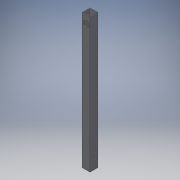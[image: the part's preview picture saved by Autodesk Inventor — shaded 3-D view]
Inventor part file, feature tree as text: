
AUTODESK INVENTOR PART (.ipt)
format: ipt  version: 2018 (Build 220112000, 112)  size: 145,408 bytes
history: native  units: in
note: dims shown in document units (in); Inventor stores cm internally (conversion verified against a paired STEP export)
features: extrude x4, sketch x4
ambient origin geometry x8: Origin, YZ Plane, XZ Plane, XY Plane, X Axis, Y Axis, Z Axis, Center Point
bodies: Solid1 (feature_tree)
feature tree (8):
  extrude  "Extrusion1"  Depth=1.0in
  extrude  "Extrusion2"  Depth=0.065in
  extrude  "Extrusion3"  Depth=0.065in
  extrude  "Extrusion4"  Depth=1.0in
  sketch  "Sketch1"  dims[d0=1.0in d1=1.0in]
  sketch  "Sketch2"  dims[d2=0.065in d3=0.065in]
  sketch  "Sketch3"  dims[d4=0.065in d5=0.065in]
  sketch  "Sketch5"  dims[d6=17.0in d7=0.0in d8=0.2031in d9=0.5in d10=0.5in d11=0.5in d12=0.2031in d13=0.2031in d14=1.0in d15=2.0in d16=1.5in d17=1.0in d18=0.0in d19=0.75in d20=2.0in d21=1.0in d22=0.0in d26=0.5in d27=0.9375in d28=0.9375in d29=0.2031in d30=0.2031in d31=0.5in d32=0.5in d33=3.0in d34=0.0in]
